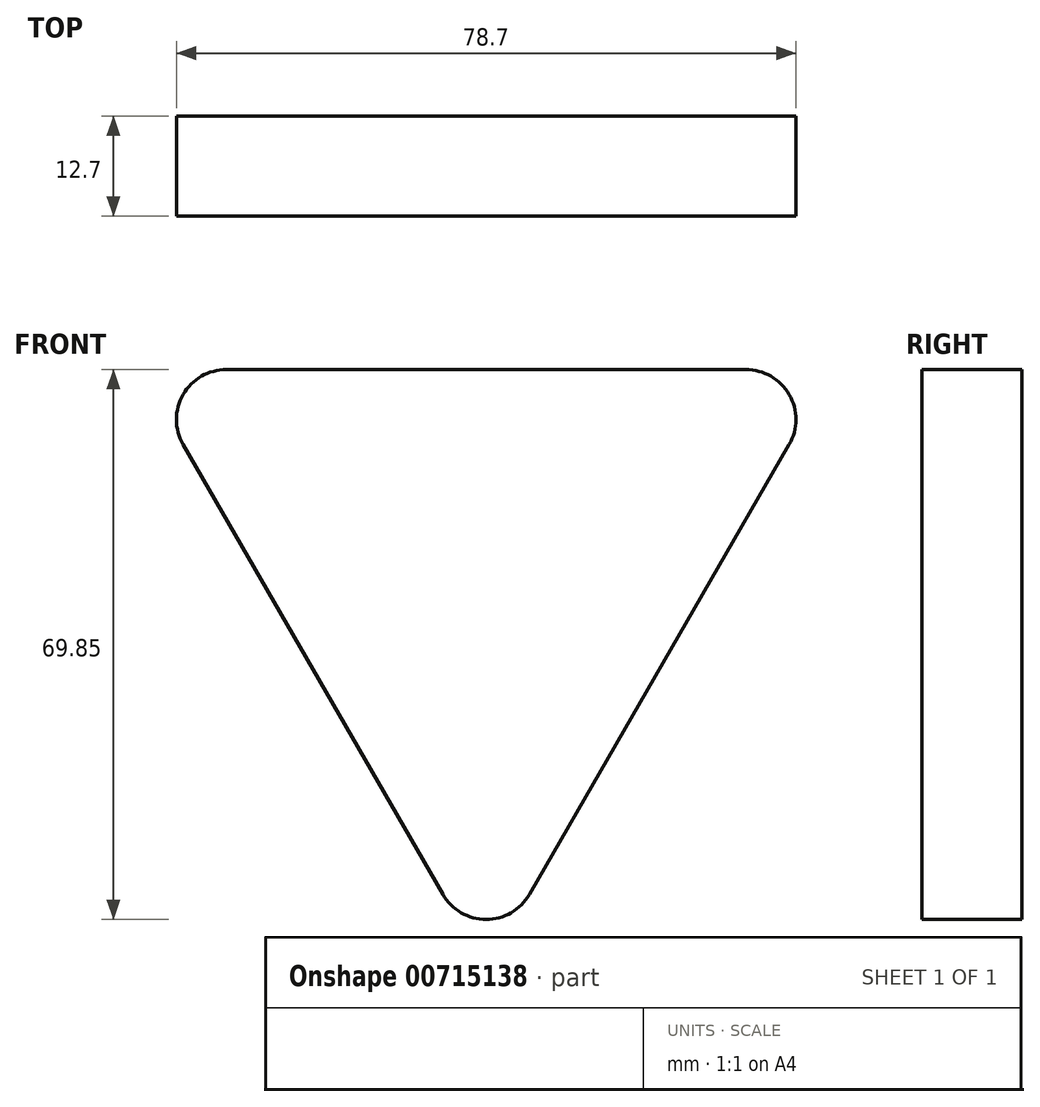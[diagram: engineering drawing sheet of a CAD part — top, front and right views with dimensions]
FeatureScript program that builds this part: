
annotation { "Feature Type Name" : "Feature", "Feature Type Description" : "" }
export const myFeature = defineFeature(function(context is Context, id is Id, definition is map)
    precondition{}
    {
        {
            var Q0;
            Q0=qCreatedBy(makeId("Front.planeOp"),FACE);
            var sketch = newSketch(context, id + "F0", { "sketchPlane" : qUnion([Q0])});
            skLineSegment(sketch, "E0", {"start": v(-33, 19.05) * mm, "end": v(33, 19.05) * mm, "construction": true});
            skLineSegment(sketch, "E1", {"start": v(33, 19.05) * mm, "end": v(0, -38.1) * mm, "construction": true});
            skLineSegment(sketch, "E2", {"start": v(0, -38.1) * mm, "end": v(-33, 19.05) * mm, "construction": true});
            skCircle(sketch, "E3", {"center": v(0, 0) * mm, "radius": 50.8 * mm, "construction": true});
            skLineSegment(sketch, "E4.0", {"start": v(-33, 25.4) * mm, "end": v(33, 25.4) * mm});
            skLineSegment(sketch, "E4.1", {"start": v(-5.5, -41.28) * mm, "end": v(-38.5, 15.88) * mm});
            skLineSegment(sketch, "E4.2", {"start": v(38.5, 15.88) * mm, "end": v(5.5, -41.27) * mm});
            skPoint(sketch, "E5.visualSharp", {"position": v(-44, 25.4) * mm});
            skArc(sketch, "E5.filletArc", {"start": v(-33, 25.4) * mm, "mid": v(-38.5, 22.23) * mm, "end": v(-38.5, 15.88) * mm});
            skPoint(sketch, "E6.visualSharp", {"position": v(44, 25.4) * mm});
            skArc(sketch, "E6.filletArc", {"start": v(38.5, 15.88) * mm, "mid": v(38.5, 22.23) * mm, "end": v(33, 25.4) * mm});
            skPoint(sketch, "E7.visualSharp", {"position": v(0, -50.8) * mm});
            skArc(sketch, "E7.filletArc", {"start": v(-5.5, -41.27) * mm, "mid": v(0, -44.45) * mm, "end": v(5.5, -41.27) * mm});
            skSolve(sketch);
        }
        {
            var Q0;
            Q0=makeQuery(id+"F0.imprint","IMPRINT",FACE,{"disambiguationData":[TD([[makeQuery(id+"F0.imprint","IMPRINT",EDGE,{"derivedFrom":sQuery(id+"F0.wireOp",EDGE,"E4.0")}),-1.0]])]});
            extrude(context, id + "F1", {"entities" : qUnion([Q0]), "depth" : 12.7 * mm});
        }
    });
